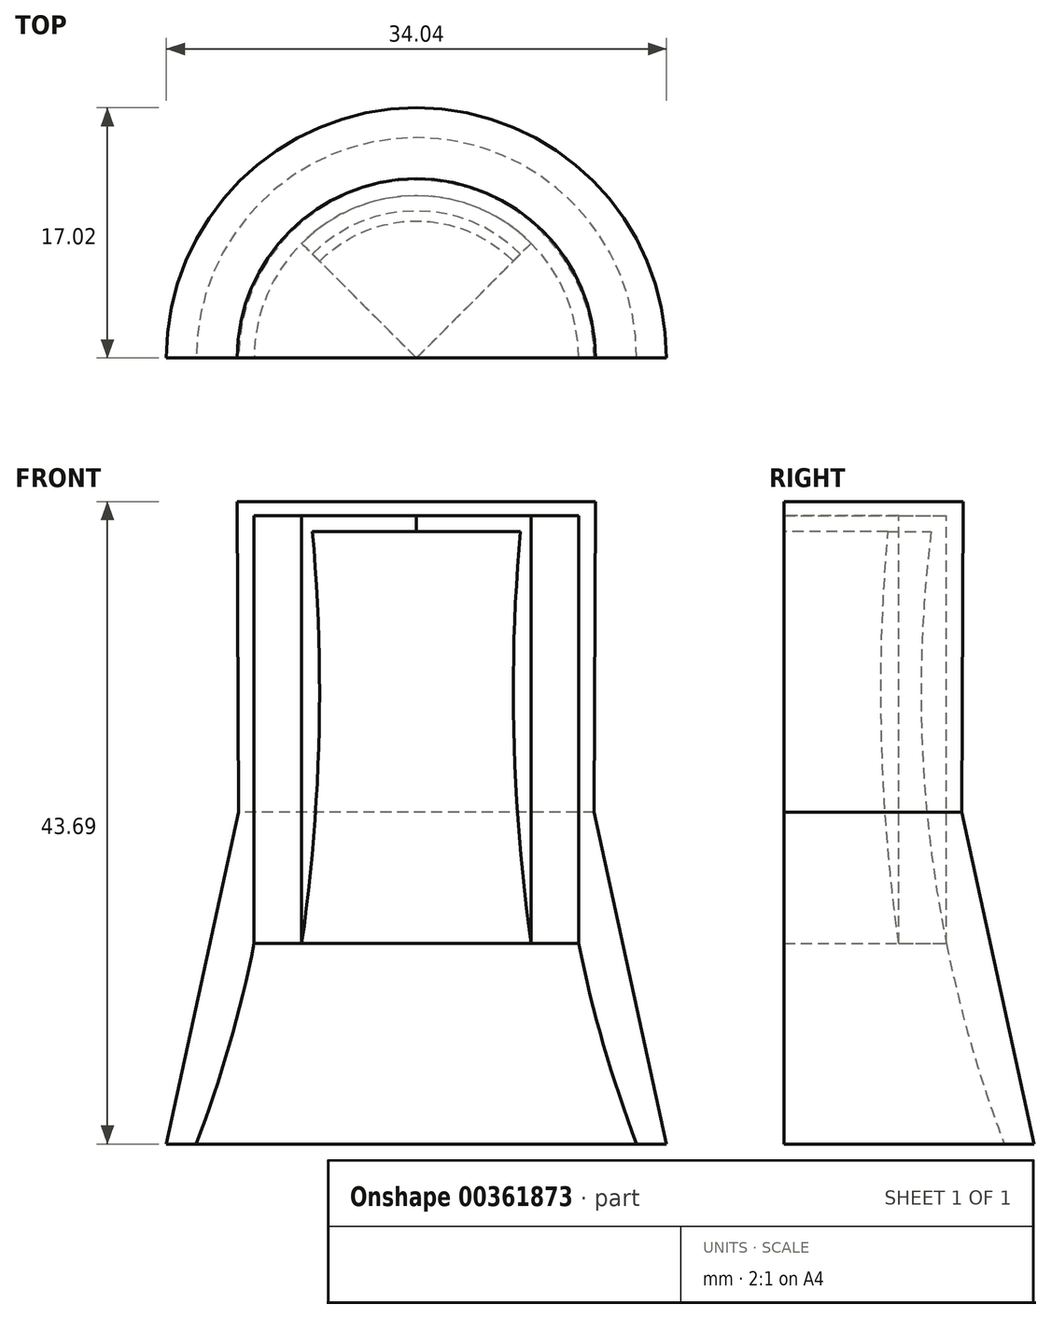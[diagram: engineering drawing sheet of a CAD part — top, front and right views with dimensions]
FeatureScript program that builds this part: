
annotation { "Feature Type Name" : "Feature", "Feature Type Description" : "" }
export const myFeature = defineFeature(function(context is Context, id is Id, definition is map)
    precondition{}
    {
        {
            var Q0;
            Q0=qCreatedBy(makeId("Front.planeOp"),FACE);
            var sketch = newSketch(context, id + "F0", { "sketchPlane" : qUnion([Q0])});
            skLineSegment(sketch, "E0", {"start": v(0, 9.22) * mm, "end": v(-12.2, 9.22) * mm});
            skLineSegment(sketch, "E1", {"start": v(0, 9.22) * mm, "end": v(0, 7.18) * mm});
            skLineSegment(sketch, "E2", {"start": v(-10, 7.18) * mm, "end": v(0, 7.18) * mm});
            skArc(sketch, "E3", {"start": v(-14.99, -34.47) * mm, "mid": v(-9.93, -13.95) * mm, "end": v(-10, 7.18) * mm});
            skLineSegment(sketch, "E4", {"start": v(-14.99, -34.47) * mm, "end": v(-17.02, -34.47) * mm});
            skLineSegment(sketch, "E5.bottom", {"start": v(0, 9.22) * mm, "end": v(-5.1, 9.22) * mm});
            skLineSegment(sketch, "E6", {"start": v(-11.04, 7.18) * mm, "end": v(-11.04, -20.84) * mm});
            skLineSegment(sketch, "E7", {"start": v(-11.04, 7.18) * mm, "end": v(-11.04, 8.26) * mm});
            skLineSegment(sketch, "E8", {"start": v(-11.04, 8.26) * mm, "end": v(0, 8.26) * mm});
            skLineSegment(sketch, "E9", {"start": v(-12.2, 9.22) * mm, "end": v(-12.1, -11.92) * mm});
            skLineSegment(sketch, "E10", {"start": v(-12.1, -11.92) * mm, "end": v(-17.02, -34.47) * mm});
            skSolve(sketch);
        }
        {
            var Q0;
            {var subQ1=sQuery(id+"F0.wireOp",EDGE,"E0");Q0=makeQuery(id+"F0.imprint","IMPRINT",FACE,{"disambiguationData":[TD([[makeQuery(id+"F0.imprint","IMPRINT",EDGE,{"derivedFrom":subQ1}),1.0]])]});}
            var Q1;
            {var subQ4=sQuery(id+"F0.wireOp",EDGE,"GP1030gZ-cmCY-5Lff-BzS9-phZB1ULsYkCb");Q1=makeQuery(id+"F0.imprint","IMPRINT",FACE,{"disambiguationData":[TD([[makeQuery(id+"F0.imprint","IMPRINT",EDGE,{"derivedFrom":subQ4}),-1.0]])]});}
            var Q2;
            {var subQ5=sQuery(id+"F0.wireOp",EDGE,"7P7h2uZu-wLRN-yOsa-oIWB-QkgRby0zkctz");Q2=makeQuery(id+"F0.imprint","IMPRINT",FACE,{"disambiguationData":[TD([[makeQuery(id+"F0.imprint","IMPRINT",EDGE,{"derivedFrom":subQ5}),-1.0]])]});}
            var Q3;
            Q3=sQuery(id+"F0.wireOp",EDGE,"E1");
            revolve(context, id + "F1", {"entities" : qUnion([Q0, Q1, Q2]), "axis" : qUnion([Q3]), "revolveType" : RevolveType.ONE_DIRECTION, "angle" : 180 * degree});
        }
        {
            var Q0;
            {var subQ1=sQuery(id+"F0.wireOp",EDGE,"E2");Q0=makeQuery(id+"F0.imprint","IMPRINT",FACE,{"disambiguationData":[TD([[makeQuery(id+"F0.imprint","IMPRINT",EDGE,{"derivedFrom":subQ1}),1.0]])]});}
            var Q1;
            Q1=sQuery(id+"F0.wireOp",EDGE,"E1");
            revolve(context, id + "F2", {"surfaceOperationType" : NewSurfaceOperationType.NEW, "entities" : qUnion([Q0]), "axis" : qUnion([Q1]), "revolveType" : RevolveType.TWO_DIRECTIONS, "angle" : 135 * degree, "angleBack" : 45 * degree});
        }
    });
